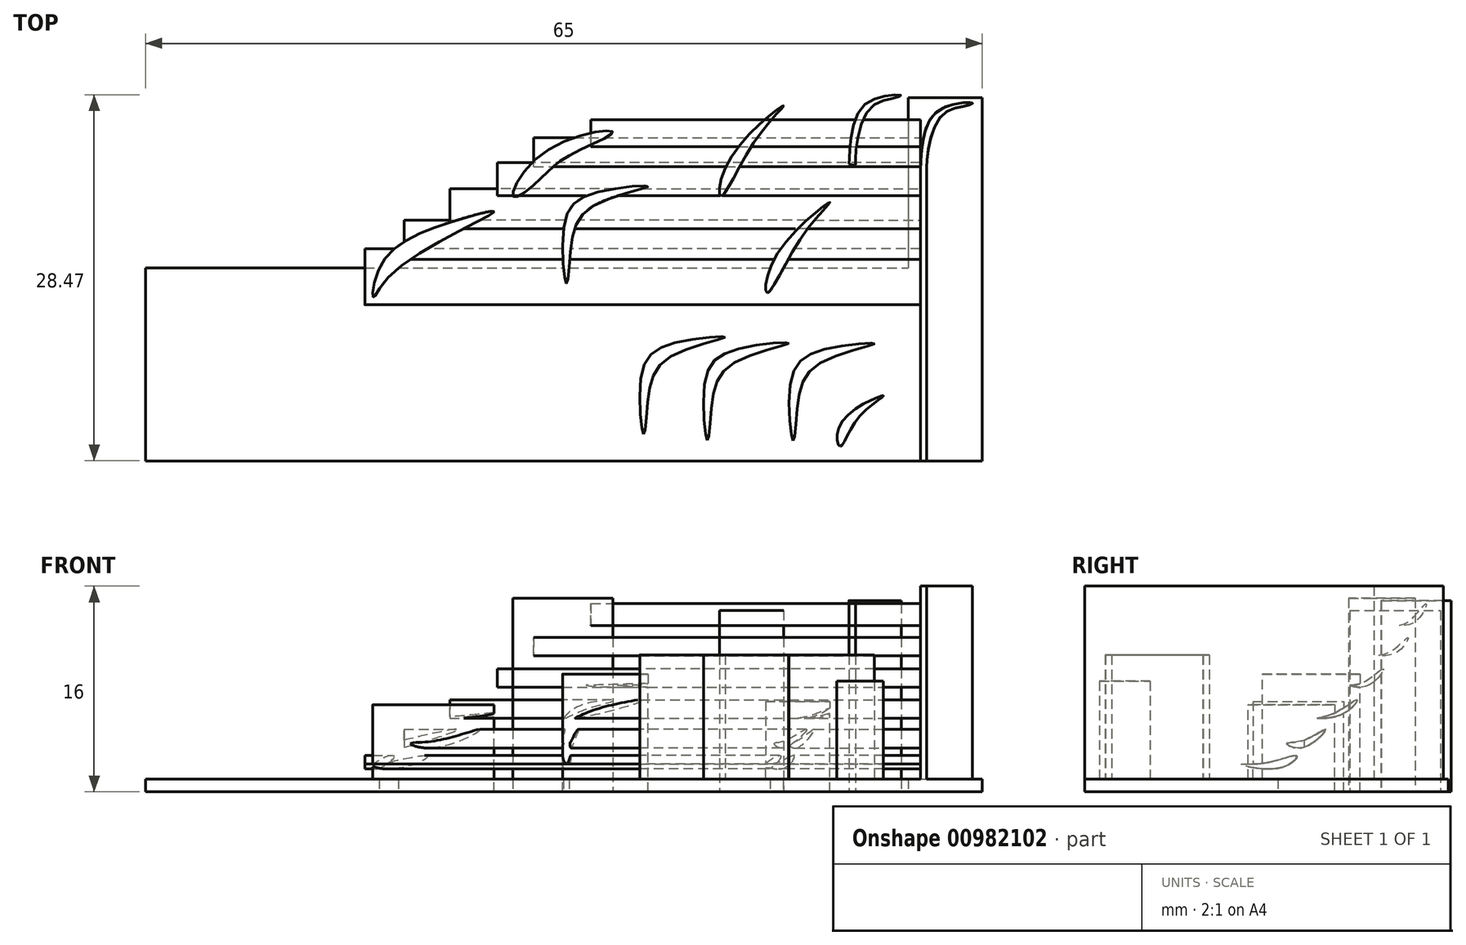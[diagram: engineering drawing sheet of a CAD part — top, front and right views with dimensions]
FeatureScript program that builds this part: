
annotation { "Feature Type Name" : "Feature", "Feature Type Description" : "" }
export const myFeature = defineFeature(function(context is Context, id is Id, definition is map)
    precondition{}
    {
        {
            var Q0;
            Q0=qCreatedBy(makeId("Top.planeOp"),FACE);
            var sketch = newSketch(context, id + "F0", { "sketchPlane" : qUnion([Q0])});
            skLineSegment(sketch, "E0.bottom", {"start": v(16.9, -1.9) * mm, "end": v(81.9, -1.9) * mm});
            skLineSegment(sketch, "E0.top", {"start": v(16.9, -16.9) * mm, "end": v(81.9, -16.9) * mm});
            skLineSegment(sketch, "E0.left", {"start": v(16.9, -1.9) * mm, "end": v(16.9, -16.9) * mm});
            skLineSegment(sketch, "E0.right", {"start": v(81.9, -1.9) * mm, "end": v(81.9, -16.9) * mm});
            skSolve(sketch);
        }
        {
            var Q0;
            Q0=makeQuery(id+"F0.imprint","IMPRINT",FACE,{"disambiguationData":[TD([[makeQuery(id+"F0.imprint","IMPRINT",EDGE,{"derivedFrom":sQuery(id+"F0.wireOp",EDGE,"E0.bottom")}),-1.0]])]});
            extrude(context, id + "F1", {"entities" : qUnion([Q0]), "depth" : 1 * mm, "offsetDistance" : 25.4 * mm});
        }
        {
            var Q0;
            Q0=makeQuery(id+"F1.opExtrude","CAP_FACE",FACE,{"disambiguationData":[OSD([sQuery(id+"F0.wireOp",EDGE,"E0.bottom"),sQuery(id+"F0.wireOp",EDGE,"E0.top"),sQuery(id+"F0.wireOp",EDGE,"E0.left"),sQuery(id+"F0.wireOp",EDGE,"E0.right")])],"isStart":false});
            var sketch = newSketch(context, id + "F2", { "sketchPlane" : qUnion([Q0])});
            skLineSegment(sketch, "E1.bottom", {"start": v(77.61, -16.9) * mm, "end": v(77.11, -16.9) * mm});
            skLineSegment(sketch, "E1.top", {"start": v(77.61, 5.6) * mm, "end": v(77.11, 5.6) * mm});
            skLineSegment(sketch, "E1.left", {"start": v(77.61, -16.9) * mm, "end": v(77.61, 5.6) * mm});
            skLineSegment(sketch, "E1.right", {"start": v(77.11, -16.9) * mm, "end": v(77.11, 5.6) * mm});
            skSolve(sketch);
        }
        {
            var Q0;
            Q0=makeQuery(id+"F1.opExtrude","SWEPT_FACE",FACE,{"disambiguationData":[OSD([sQuery(id+"F0.wireOp",EDGE,"E0.bottom")])]});
            var sketch = newSketch(context, id + "F3", { "sketchPlane" : qUnion([Q0])});
            skLineSegment(sketch, "E2.bottom", {"start": v(-81.9, 1) * mm, "end": v(-76.15, 1) * mm});
            skLineSegment(sketch, "E2.top", {"start": v(-81.9, 0) * mm, "end": v(-76.15, 0) * mm});
            skLineSegment(sketch, "E2.left", {"start": v(-81.9, 1) * mm, "end": v(-81.9, 0) * mm});
            skLineSegment(sketch, "E2.right", {"start": v(-76.15, 1) * mm, "end": v(-76.15, 0) * mm});
            skSolve(sketch);
        }
        {
            var Q0;
            Q0=makeQuery(id+"F3.imprint","IMPRINT",FACE,{"disambiguationData":[TD([[makeQuery(id+"F3.imprint","IMPRINT",EDGE,{"derivedFrom":sQuery(id+"F3.wireOp",EDGE,"E2.bottom")}),1.0]])]});
            extrude(context, id + "F4", {"entities" : qUnion([Q0]), "operationType" : NewBodyOperationType.ADD, "depth" : 13.23 * mm, "offsetDistance" : 25.4 * mm});
        }
        {
            var Q0;
            Q0=makeQuery(id+"F4.boolean.opBoolean","MERGE",FACE,{"derivedFrom":[makeQuery(id+"F1.opExtrude","CAP_FACE",FACE,{"disambiguationData":[OSD([sQuery(id+"F0.wireOp",EDGE,"E0.bottom"),sQuery(id+"F0.wireOp",EDGE,"E0.top"),sQuery(id+"F0.wireOp",EDGE,"E0.left"),sQuery(id+"F0.wireOp",EDGE,"E0.right")])],"isStart":false}),makeQuery(id+"F4.opExtrude","SWEPT_FACE",FACE,{"disambiguationData":[OSD([sQuery(id+"F3.wireOp",EDGE,"E2.bottom")])]})]});
            var sketch = newSketch(context, id + "F5", { "sketchPlane" : qUnion([Q0])});
            skFitSpline(sketch, "E3", {"points": [v(77.11, 5.6) * mm, v(77.17, 6.8) * mm, v(78.07, 9.93) * mm, v(80.35, 10.93) * mm, v(81.17, 10.9) * mm, v(80.7, 10.72) * mm, v(78.86, 10.04) * mm, v(77.67, 6.8) * mm, v(77.61, 5.6) * mm, v(77.6, 5.56) * mm, v(77.6, 5.5) * mm, v(77.5, 5.52) * mm, v(77.12, 5.54) * mm, v(77.11, 5.6) * mm]});
            skSolve(sketch);
        }
        {
            var Q0;
            Q0=makeQuery(id+"F5.imprint","IMPRINT",FACE,{"disambiguationData":[TD([[makeQuery(id+"F5.imprint","IMPRINT",EDGE,{"derivedFrom":sQuery(id+"F5.wireOp",EDGE,"E3")}),-1.0]])]});
            var Q1;
            {var subQ0=sQuery(id+"F2.wireOp",EDGE,"E1.bottom");Q1=makeQuery(id+"F2.imprint","IMPRINT",FACE,{"disambiguationData":[TD([[makeQuery(id+"F2.imprint","IMPRINT",EDGE,{"derivedFrom":subQ0}),1.0]])]});}
            var Q2;
            {var subQ0=sQuery(id+"F2.wireOp",EDGE,"E1.top");Q2=makeQuery(id+"F2.imprint","IMPRINT",FACE,{"disambiguationData":[TD([[makeQuery(id+"F2.imprint","IMPRINT",EDGE,{"derivedFrom":subQ0}),1.0]])]});}
            extrude(context, id + "F6", {"entities" : qUnion([Q0, Q1, Q2]), "operationType" : NewBodyOperationType.ADD, "depth" : 15 * mm, "offsetDistance" : 25.4 * mm});
        }
        {
            var Q0;
            Q0=makeQuery(id+"F4.boolean.opBoolean","MERGE",FACE,{"derivedFrom":[makeQuery(id+"F1.opExtrude","CAP_FACE",FACE,{"disambiguationData":[OSD([sQuery(id+"F0.wireOp",EDGE,"E0.bottom"),sQuery(id+"F0.wireOp",EDGE,"E0.top"),sQuery(id+"F0.wireOp",EDGE,"E0.left"),sQuery(id+"F0.wireOp",EDGE,"E0.right")])],"isStart":false}),makeQuery(id+"F4.opExtrude","SWEPT_FACE",FACE,{"disambiguationData":[OSD([sQuery(id+"F3.wireOp",EDGE,"E2.bottom")])]})]});
            var sketch = newSketch(context, id + "F7", { "sketchPlane" : qUnion([Q0])});
            skFitSpline(sketch, "E4", {"points": [v(55.6, -14.83) * mm, v(55.97, -11.97) * mm, v(57.8, -8.75) * mm, v(61.93, -7.29) * mm, v(57.85, -7.78) * mm, v(55.42, -10.27) * mm, v(55.6, -14.83) * mm]});
            skFitSpline(sketch, "E5", {"points": [v(60.56, -15.29) * mm, v(60.92, -12.43) * mm, v(62.74, -9.2) * mm, v(66.88, -7.75) * mm, v(62.8, -8.23) * mm, v(60.37, -10.73) * mm, v(60.56, -15.29) * mm]});
            skFitSpline(sketch, "E6", {"points": [v(67.22, -15.33) * mm, v(67.58, -12.47) * mm, v(69.4, -9.25) * mm, v(73.54, -7.8) * mm, v(69.47, -8.28) * mm, v(67.03, -10.77) * mm, v(67.22, -15.33) * mm]});
            skSolve(sketch);
        }
        {
            var Q0;
            Q0=makeQuery(id+"F7.imprint","IMPRINT",FACE,{"disambiguationData":[TD([[makeQuery(id+"F7.imprint","IMPRINT",EDGE,{"derivedFrom":sQuery(id+"F7.wireOp",EDGE,"E4")}),1.0]])]});
            var Q1;
            Q1=makeQuery(id+"F7.imprint","IMPRINT",FACE,{"disambiguationData":[TD([[makeQuery(id+"F7.imprint","IMPRINT",EDGE,{"derivedFrom":sQuery(id+"F7.wireOp",EDGE,"E5")}),1.0]])]});
            var Q2;
            Q2=makeQuery(id+"F7.imprint","IMPRINT",FACE,{"disambiguationData":[TD([[makeQuery(id+"F7.imprint","IMPRINT",EDGE,{"derivedFrom":sQuery(id+"F7.wireOp",EDGE,"E6")}),1.0]])]});
            extrude(context, id + "F8", {"entities" : qUnion([Q0, Q1, Q2]), "operationType" : NewBodyOperationType.ADD, "depth" : 9.65 * mm, "offsetDistance" : 25.4 * mm});
        }
        {
            var Q0;
            Q0=makeQuery(id+"F4.boolean.opBoolean","MERGE",FACE,{"derivedFrom":[makeQuery(id+"F1.opExtrude","CAP_FACE",FACE,{"disambiguationData":[OSD([sQuery(id+"F0.wireOp",EDGE,"E0.bottom"),sQuery(id+"F0.wireOp",EDGE,"E0.top"),sQuery(id+"F0.wireOp",EDGE,"E0.left"),sQuery(id+"F0.wireOp",EDGE,"E0.right")])],"isStart":false}),makeQuery(id+"F4.opExtrude","SWEPT_FACE",FACE,{"disambiguationData":[OSD([sQuery(id+"F3.wireOp",EDGE,"E2.bottom")])]})]});
            var sketch = newSketch(context, id + "F9", { "sketchPlane" : qUnion([Q0])});
            skFitSpline(sketch, "E7", {"points": [v(70.87, -15.78) * mm, v(70.95, -13.95) * mm, v(74.23, -11.83) * mm, v(72.26, -13.59) * mm, v(70.87, -15.78) * mm]});
            skSolve(sketch);
        }
        {
            var Q0;
            Q0=makeQuery(id+"F9.imprint","IMPRINT",FACE,{"disambiguationData":[TD([[makeQuery(id+"F9.imprint","IMPRINT",EDGE,{"derivedFrom":sQuery(id+"F9.wireOp",EDGE,"E7")}),-1.0]])]});
            extrude(context, id + "F10", {"entities" : qUnion([Q0]), "operationType" : NewBodyOperationType.ADD, "depth" : 7.62 * mm, "offsetDistance" : 25.4 * mm});
        }
        {
            var Q0;
            Q0=makeQuery(id+"F6.opExtrude","SWEPT_FACE",FACE,{"disambiguationData":[OSD([sQuery(id+"F2.wireOp",EDGE,"E1.right")])]});
            var sketch = newSketch(context, id + "F11", { "sketchPlane" : qUnion([Q0])});
            skFitSpline(sketch, "E8", {"points": [v(4.76, 2.13) * mm, v(2.97, 2.24) * mm, v(0.41, 2.8) * mm, v(1.7, 1.88) * mm, v(4.76, 2.13) * mm]});
            skFitSpline(sketch, "E9", {"points": [v(0.41, 4) * mm, v(-1.98, 4.65) * mm, v(-4.45, 6.16) * mm, v(-3.14, 4.4) * mm, v(0.41, 4) * mm]});
            skFitSpline(sketch, "E10", {"points": [v(-3.59, 6.95) * mm, v(-5.55, 7.45) * mm, v(-7.64, 8.85) * mm, v(-6.24, 7.3) * mm, v(-3.59, 6.95) * mm]});
            skFitSpline(sketch, "E11", {"points": [v(-6.94, 9.55) * mm, v(-8.39, 10) * mm, v(-10.14, 11.1) * mm, v(-8.79, 9.65) * mm, v(-6.44, 9.4) * mm, v(-6.94, 9.55) * mm]});
            skSolve(sketch);
        }
        {
            var Q0;
            Q0=makeQuery(id+"F11.imprint","IMPRINT",FACE,{"disambiguationData":[TD([[makeQuery(id+"F11.imprint","IMPRINT",EDGE,{"derivedFrom":sQuery(id+"F11.wireOp",EDGE,"E8")}),1.0]])]});
            extrude(context, id + "F12", {"entities" : qUnion([Q0]), "operationType" : NewBodyOperationType.ADD, "depth" : 43.18 * mm, "offsetDistance" : 25.4 * mm});
        }
        {
            var Q0;
            Q0=makeQuery(id+"F6.opExtrude","SWEPT_FACE",FACE,{"disambiguationData":[OSD([sQuery(id+"F2.wireOp",EDGE,"E1.right")])]});
            var sketch = newSketch(context, id + "F13", { "sketchPlane" : qUnion([Q0])});
            skFitSpline(sketch, "E12", {"points": [v(1.23, 3.77) * mm, v(0, 3.98) * mm, v(-1.82, 4.86) * mm, v(0, 3.44) * mm, v(1.23, 3.77) * mm]});
            skSolve(sketch);
        }
        {
            var Q0;
            Q0=makeQuery(id+"F13.imprint","IMPRINT",FACE,{"disambiguationData":[TD([[makeQuery(id+"F13.imprint","IMPRINT",EDGE,{"derivedFrom":sQuery(id+"F13.wireOp",EDGE,"E12")}),-1.0]])]});
            var sketch = newSketch(context, id + "F14", { "sketchPlane" : qUnion([Q0])});
            skFitSpline(sketch, "E13", {"points": [v(-1.16, 5.74) * mm, v(-2.37, 6.07) * mm, v(-4.25, 7.16) * mm, v(-3.16, 6.07) * mm, v(-1.16, 5.74) * mm]});
            skSolve(sketch);
        }
        {
            var Q0;
            Q0=makeQuery(id+"F13.imprint","IMPRINT",FACE,{"disambiguationData":[TD([[makeQuery(id+"F13.imprint","IMPRINT",EDGE,{"derivedFrom":sQuery(id+"F13.wireOp",EDGE,"E12")}),-1.0]])]});
            var sketch = newSketch(context, id + "F15", { "sketchPlane" : qUnion([Q0])});
            skFitSpline(sketch, "E14", {"points": [v(-3.7, 8.28) * mm, v(-4.58, 8.45) * mm, v(-6.3, 9.58) * mm, v(-5.12, 8.28) * mm, v(-3.7, 8.28) * mm]});
            skSolve(sketch);
        }
        {
            var Q0;
            Q0=makeQuery(id+"F13.imprint","IMPRINT",FACE,{"disambiguationData":[TD([[makeQuery(id+"F13.imprint","IMPRINT",EDGE,{"derivedFrom":sQuery(id+"F13.wireOp",EDGE,"E12")}),-1.0]])]});
            var sketch = newSketch(context, id + "F16", { "sketchPlane" : qUnion([Q0])});
            skFitSpline(sketch, "E15", {"points": [v(-5.96, 10.62) * mm, v(-6.84, 10.92) * mm, v(-8.21, 12) * mm, v(-7.3, 10.83) * mm, v(-5.96, 10.62) * mm]});
            skSolve(sketch);
        }
        {
            var Q0;
            Q0=makeQuery(id+"F13.imprint","IMPRINT",FACE,{"disambiguationData":[TD([[makeQuery(id+"F13.imprint","IMPRINT",EDGE,{"derivedFrom":sQuery(id+"F13.wireOp",EDGE,"E12")}),-1.0]])]});
            var sketch = newSketch(context, id + "F17", { "sketchPlane" : qUnion([Q0])});
            skFitSpline(sketch, "E16", {"points": [v(-7.53, 12.97) * mm, v(-8.18, 13.2) * mm, v(-9.62, 14.63) * mm, v(-8.74, 13.2) * mm, v(-7.53, 12.97) * mm]});
            skSolve(sketch);
        }
        {
            var Q0;
            Q0=makeQuery(id+"F13.imprint","IMPRINT",FACE,{"disambiguationData":[TD([[makeQuery(id+"F13.imprint","IMPRINT",EDGE,{"derivedFrom":sQuery(id+"F13.wireOp",EDGE,"E12")}),1.0]])]});
            extrude(context, id + "F18", {"entities" : qUnion([Q0]), "operationType" : NewBodyOperationType.ADD, "depth" : 40.13 * mm, "offsetDistance" : 25.4 * mm});
        }
        {
            var Q0;
            Q0=makeQuery(id+"F14.imprint","IMPRINT",FACE,{"disambiguationData":[TD([[makeQuery(id+"F14.imprint","IMPRINT",EDGE,{"derivedFrom":sQuery(id+"F14.wireOp",EDGE,"E13")}),1.0]])]});
            extrude(context, id + "F19", {"entities" : qUnion([Q0]), "operationType" : NewBodyOperationType.ADD, "depth" : 36.58 * mm, "offsetDistance" : 25.4 * mm});
        }
        {
            var Q0;
            {var subQ0=sQuery(id+"F15.wireOp",EDGE,"E14");var subQ1=makeQuery(id+"F13.imprint","IMPRINT",EDGE,{"derivedFrom":makeQuery(id+"F6.boolean.opBoolean","INTERSECT",EDGE,{"derivedFrom":[makeQuery(id+"F6.opExtrude","SWEPT_FACE",FACE,{"disambiguationData":[OSD([sQuery(id+"F2.wireOp",EDGE,"E1.right")])]}),makeQuery(id+"F6.opExtrude","SWEPT_FACE",FACE,{"disambiguationData":[OSD([sQuery(id+"F5.wireOp",EDGE,"E3")])]})]})});var subQ2=makeQuery(id+"F15.imprint","INTERSECT",VERTEX,{"disambiguationData":[OD(0.0)],"derivedFrom":[subQ1,subQ0]});Q0=makeQuery(id+"F15.imprint","IMPRINT",FACE,{"disambiguationData":[TD([[makeQuery(id+"F15.imprint","IMPRINT",EDGE,{"disambiguationData":[TD([[subQ2,1.0]])],"derivedFrom":subQ0}),1.0]])]});}
            var Q1;
            {var subQ0=sQuery(id+"F15.wireOp",EDGE,"E14");var subQ1=makeQuery(id+"F13.imprint","IMPRINT",EDGE,{"derivedFrom":makeQuery(id+"F6.boolean.opBoolean","INTERSECT",EDGE,{"derivedFrom":[makeQuery(id+"F6.opExtrude","SWEPT_FACE",FACE,{"disambiguationData":[OSD([sQuery(id+"F2.wireOp",EDGE,"E1.right")])]}),makeQuery(id+"F6.opExtrude","SWEPT_FACE",FACE,{"disambiguationData":[OSD([sQuery(id+"F5.wireOp",EDGE,"E3")])]})]})});var subQ2=makeQuery(id+"F15.imprint","INTERSECT",VERTEX,{"disambiguationData":[OD(0.0)],"derivedFrom":[subQ1,subQ0]});Q1=makeQuery(id+"F15.imprint","IMPRINT",FACE,{"disambiguationData":[TD([[makeQuery(id+"F15.imprint","IMPRINT",EDGE,{"disambiguationData":[TD([[subQ2,-1.0]])],"derivedFrom":subQ0}),1.0]])]});}
            extrude(context, id + "F20", {"entities" : qUnion([Q0, Q1]), "operationType" : NewBodyOperationType.ADD, "depth" : 32.87 * mm, "offsetDistance" : 25.4 * mm});
        }
        {
            var Q0;
            Q0=makeQuery(id+"F16.imprint","IMPRINT",FACE,{"disambiguationData":[TD([[makeQuery(id+"F16.imprint","IMPRINT",EDGE,{"derivedFrom":sQuery(id+"F16.wireOp",EDGE,"E15")}),1.0]])]});
            extrude(context, id + "F21", {"entities" : qUnion([Q0]), "depth" : 30.05 * mm, "offsetDistance" : 25.4 * mm});
        }
        {
            var Q0;
            Q0=makeQuery(id+"F17.imprint","IMPRINT",FACE,{"disambiguationData":[TD([[makeQuery(id+"F17.imprint","IMPRINT",EDGE,{"derivedFrom":sQuery(id+"F17.wireOp",EDGE,"E16")}),1.0]])]});
            extrude(context, id + "F22", {"entities" : qUnion([Q0]), "depth" : 25.6 * mm, "offsetDistance" : 25.4 * mm});
        }
        {
            var Q0;
            Q0=qCreatedBy(makeId("Top.planeOp"),FACE);
            var sketch = newSketch(context, id + "F23", { "sketchPlane" : qUnion([Q0])});
            skFitSpline(sketch, "E17", {"points": [v(49.6, -3.1) * mm, v(49.97, -0.25) * mm, v(51.8, 2.98) * mm, v(55.93, 4.44) * mm, v(51.86, 3.95) * mm, v(49.42, 1.46) * mm, v(49.6, -3.1) * mm]});
            skSolve(sketch);
        }
        {
            var Q0;
            Q0=makeQuery(id+"F23.imprint","IMPRINT",FACE,{"disambiguationData":[TD([[makeQuery(id+"F23.imprint","IMPRINT",EDGE,{"derivedFrom":sQuery(id+"F23.wireOp",EDGE,"E17")}),1.0]])]});
            extrude(context, id + "F24", {"entities" : qUnion([Q0]), "operationType" : NewBodyOperationType.ADD, "depth" : 9.17 * mm, "offsetDistance" : 25.4 * mm});
        }
        {
            var Q0;
            Q0=qCreatedBy(makeId("Top.planeOp"),FACE);
            var sketch = newSketch(context, id + "F25", { "sketchPlane" : qUnion([Q0])});
            skFitSpline(sketch, "E18", {"points": [v(34.58, -4.2) * mm, v(36.1, -2.28) * mm, v(43.96, 2.45) * mm, v(40.68, 1.68) * mm, v(35.27, -1.52) * mm, v(34.58, -4.2) * mm]});
            skSolve(sketch);
        }
        {
            var Q0;
            Q0=makeQuery(id+"F25.imprint","IMPRINT",FACE,{"disambiguationData":[TD([[makeQuery(id+"F25.imprint","IMPRINT",EDGE,{"derivedFrom":sQuery(id+"F25.wireOp",EDGE,"E18")}),1.0]])]});
            extrude(context, id + "F26", {"entities" : qUnion([Q0]), "operationType" : NewBodyOperationType.ADD, "depth" : 6.78 * mm, "offsetDistance" : 25.4 * mm});
        }
        {
            var Q0;
            Q0=qCreatedBy(makeId("Top.planeOp"),FACE);
            var sketch = newSketch(context, id + "F27", { "sketchPlane" : qUnion([Q0])});
            skFitSpline(sketch, "E19", {"points": [v(47.64, 5.07) * mm, v(49.78, 6.82) * mm, v(53.2, 8.65) * mm, v(47.94, 7.13) * mm, v(45.5, 3.62) * mm, v(47.64, 5.07) * mm]});
            skSolve(sketch);
        }
        {
            var Q0;
            Q0=makeQuery(id+"F27.imprint","IMPRINT",FACE,{"disambiguationData":[TD([[makeQuery(id+"F27.imprint","IMPRINT",EDGE,{"derivedFrom":sQuery(id+"F27.wireOp",EDGE,"E19")}),1.0]])]});
            extrude(context, id + "F28", {"entities" : qUnion([Q0]), "depth" : 15.06 * mm, "offsetDistance" : 25.4 * mm});
        }
        {
            var Q0;
            Q0=qCreatedBy(makeId("Top.planeOp"),FACE);
            var sketch = newSketch(context, id + "F29", { "sketchPlane" : qUnion([Q0])});
            skFitSpline(sketch, "E20", {"points": [v(71.57, 6.2) * mm, v(71.63, 7.4) * mm, v(72.53, 10.54) * mm, v(74.8, 11.54) * mm, v(75.62, 11.51) * mm, v(75.16, 11.32) * mm, v(73.31, 10.65) * mm, v(72.12, 7.4) * mm, v(72.07, 6.2) * mm, v(72.06, 6.17) * mm, v(72.05, 6.11) * mm, v(71.96, 6.13) * mm, v(71.58, 6.15) * mm, v(71.57, 6.2) * mm]});
            skSolve(sketch);
        }
        {
            var Q0;
            Q0=makeQuery(id+"F29.imprint","IMPRINT",FACE,{"disambiguationData":[TD([[makeQuery(id+"F29.imprint","IMPRINT",EDGE,{"derivedFrom":sQuery(id+"F29.wireOp",EDGE,"E20")}),-1.0]])]});
            extrude(context, id + "F30", {"entities" : qUnion([Q0]), "depth" : 14.88 * mm, "offsetDistance" : 25.4 * mm});
        }
        {
            var Q0;
            Q0=qCreatedBy(makeId("Top.planeOp"),FACE);
            var sketch = newSketch(context, id + "F31", { "sketchPlane" : qUnion([Q0])});
            skFitSpline(sketch, "E21", {"points": [v(61.63, 3.68) * mm, v(62.3, 6.56) * mm, v(66.46, 10.72) * mm, v(64.38, 8.15) * mm, v(61.63, 3.68) * mm]});
            skSolve(sketch);
        }
        {
            var Q0;
            Q0=qCreatedBy(makeId("Top.planeOp"),FACE);
            var sketch = newSketch(context, id + "F32", { "sketchPlane" : qUnion([Q0])});
            skFitSpline(sketch, "E22", {"points": [v(65.22, -3.84) * mm, v(65.9, -0.96) * mm, v(70.06, 3.2) * mm, v(67.98, 0.63) * mm, v(65.22, -3.84) * mm]});
            skSolve(sketch);
        }
        {
            var Q0;
            Q0=makeQuery(id+"F32.imprint","IMPRINT",FACE,{"disambiguationData":[TD([[makeQuery(id+"F32.imprint","IMPRINT",EDGE,{"derivedFrom":sQuery(id+"F32.wireOp",EDGE,"E22")}),-1.0]])]});
            extrude(context, id + "F33", {"entities" : qUnion([Q0]), "operationType" : NewBodyOperationType.ADD, "depth" : 7.04 * mm, "offsetDistance" : 25.4 * mm});
        }
        {
            var Q0;
            Q0=makeQuery(id+"F31.imprint","IMPRINT",FACE,{"disambiguationData":[TD([[makeQuery(id+"F31.imprint","IMPRINT",EDGE,{"derivedFrom":sQuery(id+"F31.wireOp",EDGE,"E21")}),-1.0]])]});
            extrude(context, id + "F34", {"entities" : qUnion([Q0]), "depth" : 14.1 * mm, "offsetDistance" : 25.4 * mm});
        }
    });
